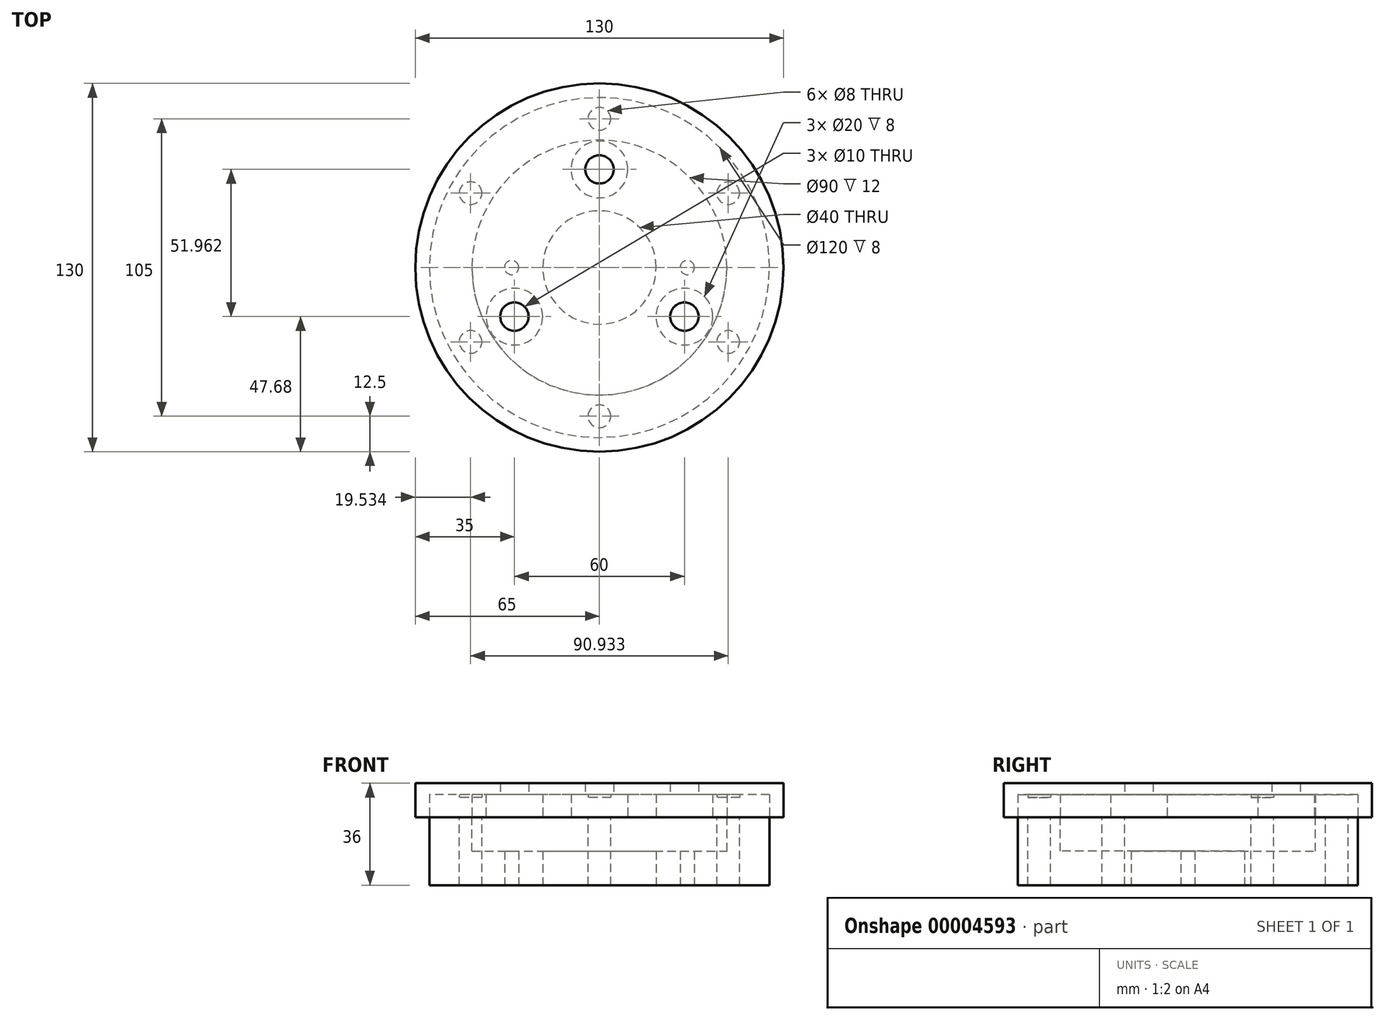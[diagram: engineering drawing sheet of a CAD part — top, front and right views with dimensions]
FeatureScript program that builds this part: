
annotation { "Feature Type Name" : "Feature", "Feature Type Description" : "" }
export const myFeature = defineFeature(function(context is Context, id is Id, definition is map)
    precondition{}
    {
        {
            var Q0;
            Q0=qCreatedBy(makeId("Top.planeOp"),FACE);
            var sketch = newSketch(context, id + "F0", { "sketchPlane" : qUnion([Q0])});
            skCircle(sketch, "E0", {"center": v(0, 0) * mm, "radius": 65 * mm});
            skLineSegment(sketch, "E1", {"start": v(0, 0) * mm, "end": v(0, 65) * mm, "construction": true});
            skLineSegment(sketch, "E2", {"start": v(0, 0) * mm, "end": v(56.3, -32.5) * mm, "construction": true});
            skLineSegment(sketch, "E3", {"start": v(0, 0) * mm, "end": v(-56.3, -32.5) * mm, "construction": true});
            skCircle(sketch, "E4", {"center": v(0, 0) * mm, "radius": 34.64 * mm, "construction": true});
            skCircle(sketch, "E5", {"center": v(0, 34.64) * mm, "radius": 5 * mm});
            skCircle(sketch, "E6", {"center": v(30, -17.32) * mm, "radius": 5 * mm});
            skCircle(sketch, "E7", {"center": v(-30, -17.32) * mm, "radius": 5 * mm});
            skCircle(sketch, "E8", {"center": v(0, 0) * mm, "radius": 60 * mm});
            skCircle(sketch, "E9", {"center": v(0, 0) * mm, "radius": 45 * mm});
            skCircle(sketch, "E10", {"center": v(-45.47, -26.25) * mm, "radius": 4 * mm});
            skCircle(sketch, "E11", {"center": v(0, 52.5) * mm, "radius": 4 * mm});
            skCircle(sketch, "E12", {"center": v(45.47, -26.25) * mm, "radius": 4 * mm});
            skCircle(sketch, "E13", {"center": v(0, 0) * mm, "radius": 52.5 * mm, "construction": true});
            skCircle(sketch, "E14", {"center": v(-52.5, 0) * mm, "radius": 7.5 * mm, "construction": true});
            skLineSegment(sketch, "E15", {"start": v(0, 0) * mm, "end": v(56.3, 32.5) * mm, "construction": true});
            skLineSegment(sketch, "E16", {"start": v(0, 0) * mm, "end": v(-56.3, 32.5) * mm, "construction": true});
            skLineSegment(sketch, "E17", {"start": v(0, 0) * mm, "end": v(0, -65) * mm, "construction": true});
            skCircle(sketch, "E18", {"center": v(45.47, 26.25) * mm, "radius": 4 * mm});
            skCircle(sketch, "E19", {"center": v(-45.47, 26.25) * mm, "radius": 4 * mm});
            skCircle(sketch, "E20", {"center": v(0, -52.5) * mm, "radius": 4 * mm});
            skCircle(sketch, "E21", {"center": v(30, -17.32) * mm, "radius": 10 * mm});
            skCircle(sketch, "E22", {"center": v(-30, -17.32) * mm, "radius": 10 * mm});
            skCircle(sketch, "E23", {"center": v(0, 34.64) * mm, "radius": 10 * mm});
            skSolve(sketch);
        }
        {
            var Q0;
            Q0=makeQuery(id+"F0.imprint","IMPRINT",FACE,{"disambiguationData":[TD([[makeQuery(id+"F0.imprint","IMPRINT",EDGE,{"derivedFrom":sQuery(id+"F0.wireOp",EDGE,"E0")}),1.0]])]});
            var Q1;
            Q1=makeQuery(id+"F0.imprint","IMPRINT",FACE,{"disambiguationData":[TD([[makeQuery(id+"F0.imprint","IMPRINT",EDGE,{"derivedFrom":sQuery(id+"F0.wireOp",EDGE,"E8")}),1.0]])]});
            var Q2;
            Q2=makeQuery(id+"F0.imprint","IMPRINT",FACE,{"disambiguationData":[TD([[makeQuery(id+"F0.imprint","IMPRINT",EDGE,{"derivedFrom":sQuery(id+"F0.wireOp",EDGE,"E5")}),-1.0]])]});
            var Q3;
            Q3=makeQuery(id+"F0.imprint","IMPRINT",FACE,{"disambiguationData":[TD([[makeQuery(id+"F0.imprint","IMPRINT",EDGE,{"derivedFrom":sQuery(id+"F0.wireOp",EDGE,"E10")}),1.0]])]});
            var Q4;
            Q4=makeQuery(id+"F0.imprint","IMPRINT",FACE,{"disambiguationData":[TD([[makeQuery(id+"F0.imprint","IMPRINT",EDGE,{"derivedFrom":sQuery(id+"F0.wireOp",EDGE,"E12")}),1.0]])]});
            var Q5;
            Q5=makeQuery(id+"F0.imprint","IMPRINT",FACE,{"disambiguationData":[TD([[makeQuery(id+"F0.imprint","IMPRINT",EDGE,{"derivedFrom":sQuery(id+"F0.wireOp",EDGE,"E11")}),1.0]])]});
            var Q6;
            Q6=makeQuery(id+"F0.imprint","IMPRINT",FACE,{"disambiguationData":[TD([[makeQuery(id+"F0.imprint","IMPRINT",EDGE,{"derivedFrom":sQuery(id+"F0.wireOp",EDGE,"E19")}),1.0]])]});
            var Q7;
            Q7=makeQuery(id+"F0.imprint","IMPRINT",FACE,{"disambiguationData":[TD([[makeQuery(id+"F0.imprint","IMPRINT",EDGE,{"derivedFrom":sQuery(id+"F0.wireOp",EDGE,"E18")}),1.0]])]});
            var Q8;
            Q8=makeQuery(id+"F0.imprint","IMPRINT",FACE,{"disambiguationData":[TD([[makeQuery(id+"F0.imprint","IMPRINT",EDGE,{"derivedFrom":sQuery(id+"F0.wireOp",EDGE,"E20")}),1.0]])]});
            var Q9;
            {var subQ0=sQuery(id+"F0.wireOp",EDGE,"E23");var subQ1=sQuery(id+"F0.wireOp",EDGE,"E9");var subQ3=makeQuery(id+"F0.imprint","INTERSECT",VERTEX,{"disambiguationData":[OD(0.0)],"derivedFrom":[subQ1,subQ0]});Q9=makeQuery(id+"F0.imprint","IMPRINT",FACE,{"disambiguationData":[TD([[makeQuery(id+"F0.imprint","IMPRINT",EDGE,{"disambiguationData":[TD([[subQ3,-1.0]])],"derivedFrom":subQ1}),1.0]])]});}
            var Q10;
            {var subQ0=sQuery(id+"F0.wireOp",EDGE,"E23");var subQ3=sQuery(id+"F0.wireOp",EDGE,"E9");var subQ4=makeQuery(id+"F0.imprint","INTERSECT",VERTEX,{"disambiguationData":[OD(0.0)],"derivedFrom":[subQ3,subQ0]});Q10=makeQuery(id+"F0.imprint","IMPRINT",FACE,{"disambiguationData":[TD([[makeQuery(id+"F0.imprint","IMPRINT",EDGE,{"disambiguationData":[TD([[subQ4,1.0]])],"derivedFrom":subQ3}),-1.0]])]});}
            var Q11;
            Q11=makeQuery(id+"F0.imprint","IMPRINT",FACE,{"disambiguationData":[TD([[makeQuery(id+"F0.imprint","IMPRINT",EDGE,{"derivedFrom":sQuery(id+"F0.wireOp",EDGE,"E7")}),-1.0]])]});
            var Q12;
            {var subQ0=sQuery(id+"F0.wireOp",EDGE,"E22");var subQ3=sQuery(id+"F0.wireOp",EDGE,"E9");var subQ6=makeQuery(id+"F0.imprint","INTERSECT",VERTEX,{"disambiguationData":[OD(0.0)],"derivedFrom":[subQ3,subQ0]});Q12=makeQuery(id+"F0.imprint","IMPRINT",FACE,{"disambiguationData":[TD([[makeQuery(id+"F0.imprint","IMPRINT",EDGE,{"disambiguationData":[TD([[subQ6,-1.0]])],"derivedFrom":subQ3}),-1.0]])]});}
            var Q13;
            Q13=makeQuery(id+"F0.imprint","IMPRINT",FACE,{"disambiguationData":[TD([[makeQuery(id+"F0.imprint","IMPRINT",EDGE,{"derivedFrom":sQuery(id+"F0.wireOp",EDGE,"E6")}),-1.0]])]});
            var Q14;
            {var subQ0=sQuery(id+"F0.wireOp",EDGE,"E21");var subQ3=sQuery(id+"F0.wireOp",EDGE,"E9");var subQ6=makeQuery(id+"F0.imprint","INTERSECT",VERTEX,{"disambiguationData":[OD(0.0)],"derivedFrom":[subQ3,subQ0]});Q14=makeQuery(id+"F0.imprint","IMPRINT",FACE,{"disambiguationData":[TD([[makeQuery(id+"F0.imprint","IMPRINT",EDGE,{"disambiguationData":[TD([[subQ6,-1.0]])],"derivedFrom":subQ3}),-1.0]])]});}
            var Q15;
            Q15=makeQuery(id+"F0.imprint","IMPRINT",FACE,{"disambiguationData":[TD([[makeQuery(id+"F0.imprint","IMPRINT",EDGE,{"derivedFrom":sQuery(id+"F0.wireOp",EDGE,"E9")}),1.0]])]});
            extrude(context, id + "F1", {"entities" : qUnion([Q0, Q1, Q2, Q3, Q4, Q5, Q6, Q7, Q8, Q9, Q10, Q11, Q12, Q13, Q14, Q15]), "depth" : 12 * mm});
        }
        {
            var Q0;
            Q0=makeQuery(id+"F0.imprint","IMPRINT",FACE,{"disambiguationData":[TD([[makeQuery(id+"F0.imprint","IMPRINT",EDGE,{"derivedFrom":sQuery(id+"F0.wireOp",EDGE,"E8")}),1.0]])]});
            extrude(context, id + "F2", {"entities" : qUnion([Q0]), "oppositeDirection" : true, "depth" : 24 * mm});
        }
        {
            var Q0;
            Q0=makeQuery(id+"F2.opExtrude","CAP_FACE",FACE,{"disambiguationData":[OSD([sQuery(id+"F0.wireOp",EDGE,"E8"),sQuery(id+"F0.wireOp",EDGE,"E9")])],"isStart":false});
            var sketch = newSketch(context, id + "F3", { "sketchPlane" : qUnion([Q0])});
            skCircle(sketch, "E24", {"center": v(-31, 0) * mm, "radius": 2.5 * mm});
            skCircle(sketch, "E25", {"center": v(31, 0) * mm, "radius": 2.5 * mm});
            skCircle(sketch, "E26", {"center": v(0, 0) * mm, "radius": 20 * mm});
            skCircle(sketch, "E27", {"center": v(0, 0) * mm, "radius": 45.5 * mm});
            skSolve(sketch);
        }
        {
            var Q0;
            Q0 = qSketchRegion(id + "F3", true);
            extrude(context, id + "F4", {"entities" : qUnion([Q0]), "operationType" : NewBodyOperationType.ADD, "oppositeDirection" : true, "depth" : 12 * mm});
        }
        {
            var Q0;
            Q0=makeQuery(id+"F0.imprint","IMPRINT",FACE,{"disambiguationData":[TD([[makeQuery(id+"F0.imprint","IMPRINT",EDGE,{"derivedFrom":sQuery(id+"F0.wireOp",EDGE,"E18")}),1.0]])]});
            var Q1;
            Q1=makeQuery(id+"F0.imprint","IMPRINT",FACE,{"disambiguationData":[TD([[makeQuery(id+"F0.imprint","IMPRINT",EDGE,{"derivedFrom":sQuery(id+"F0.wireOp",EDGE,"E11")}),1.0]])]});
            var Q2;
            Q2=makeQuery(id+"F0.imprint","IMPRINT",FACE,{"disambiguationData":[TD([[makeQuery(id+"F0.imprint","IMPRINT",EDGE,{"derivedFrom":sQuery(id+"F0.wireOp",EDGE,"E19")}),1.0]])]});
            var Q3;
            Q3=makeQuery(id+"F0.imprint","IMPRINT",FACE,{"disambiguationData":[TD([[makeQuery(id+"F0.imprint","IMPRINT",EDGE,{"derivedFrom":sQuery(id+"F0.wireOp",EDGE,"E10")}),1.0]])]});
            var Q4;
            Q4=makeQuery(id+"F0.imprint","IMPRINT",FACE,{"disambiguationData":[TD([[makeQuery(id+"F0.imprint","IMPRINT",EDGE,{"derivedFrom":sQuery(id+"F0.wireOp",EDGE,"E20")}),1.0]])]});
            var Q5;
            Q5=makeQuery(id+"F0.imprint","IMPRINT",FACE,{"disambiguationData":[TD([[makeQuery(id+"F0.imprint","IMPRINT",EDGE,{"derivedFrom":sQuery(id+"F0.wireOp",EDGE,"E12")}),1.0]])]});
            var Q6;
            Q6=sQuery(id+"F0.wireOp",EDGE,"E10");
            extrude(context, id + "F5", {"entities" : qUnion([Q0, Q1, Q2, Q3, Q4, Q5]), "operationType" : NewBodyOperationType.REMOVE, "surfaceEntities" : qUnion([Q6]), "depth" : (12 - 5) * mm});
        }
        {
            var Q0;
            Q0=makeQuery(id+"F0.imprint","IMPRINT",FACE,{"disambiguationData":[TD([[makeQuery(id+"F0.imprint","IMPRINT",EDGE,{"derivedFrom":sQuery(id+"F0.wireOp",EDGE,"E5")}),-1.0]])]});
            var Q1;
            {var subQ0=sQuery(id+"F0.wireOp",EDGE,"E23");var subQ3=sQuery(id+"F0.wireOp",EDGE,"E9");var subQ4=makeQuery(id+"F0.imprint","INTERSECT",VERTEX,{"disambiguationData":[OD(0.0)],"derivedFrom":[subQ3,subQ0]});Q1=makeQuery(id+"F0.imprint","IMPRINT",FACE,{"disambiguationData":[TD([[makeQuery(id+"F0.imprint","IMPRINT",EDGE,{"disambiguationData":[TD([[subQ4,1.0]])],"derivedFrom":subQ3}),-1.0]])]});}
            var Q2;
            Q2=makeQuery(id+"F0.imprint","IMPRINT",FACE,{"disambiguationData":[TD([[makeQuery(id+"F0.imprint","IMPRINT",EDGE,{"derivedFrom":sQuery(id+"F0.wireOp",EDGE,"E6")}),-1.0]])]});
            var Q3;
            {var subQ0=sQuery(id+"F0.wireOp",EDGE,"E21");var subQ3=sQuery(id+"F0.wireOp",EDGE,"E9");var subQ6=makeQuery(id+"F0.imprint","INTERSECT",VERTEX,{"disambiguationData":[OD(0.0)],"derivedFrom":[subQ3,subQ0]});Q3=makeQuery(id+"F0.imprint","IMPRINT",FACE,{"disambiguationData":[TD([[makeQuery(id+"F0.imprint","IMPRINT",EDGE,{"disambiguationData":[TD([[subQ6,-1.0]])],"derivedFrom":subQ3}),-1.0]])]});}
            var Q4;
            Q4=makeQuery(id+"F0.imprint","IMPRINT",FACE,{"disambiguationData":[TD([[makeQuery(id+"F0.imprint","IMPRINT",EDGE,{"derivedFrom":sQuery(id+"F0.wireOp",EDGE,"E7")}),-1.0]])]});
            var Q5;
            {var subQ0=sQuery(id+"F0.wireOp",EDGE,"E22");var subQ3=sQuery(id+"F0.wireOp",EDGE,"E9");var subQ6=makeQuery(id+"F0.imprint","INTERSECT",VERTEX,{"disambiguationData":[OD(0.0)],"derivedFrom":[subQ3,subQ0]});Q5=makeQuery(id+"F0.imprint","IMPRINT",FACE,{"disambiguationData":[TD([[makeQuery(id+"F0.imprint","IMPRINT",EDGE,{"disambiguationData":[TD([[subQ6,-1.0]])],"derivedFrom":subQ3}),-1.0]])]});}
            var Q6;
            {var subQ0=sQuery(id+"F0.wireOp",EDGE,"E22");var subQ1=sQuery(id+"F0.wireOp",EDGE,"E10");var subQ3=makeQuery(id+"F0.imprint","INTERSECT",VERTEX,{"disambiguationData":[OD(0.0)],"derivedFrom":[subQ1,subQ0]});Q6=makeQuery(id+"F0.imprint","IMPRINT",FACE,{"disambiguationData":[TD([[makeQuery(id+"F0.imprint","IMPRINT",EDGE,{"disambiguationData":[TD([[subQ3,1.0]])],"derivedFrom":subQ1}),1.0]])]});}
            var Q7;
            {var subQ0=sQuery(id+"F0.wireOp",EDGE,"E23");var subQ1=sQuery(id+"F0.wireOp",EDGE,"E11");var subQ3=makeQuery(id+"F0.imprint","INTERSECT",VERTEX,{"disambiguationData":[OD(0.0)],"derivedFrom":[subQ1,subQ0]});Q7=makeQuery(id+"F0.imprint","IMPRINT",FACE,{"disambiguationData":[TD([[makeQuery(id+"F0.imprint","IMPRINT",EDGE,{"disambiguationData":[TD([[subQ3,1.0]])],"derivedFrom":subQ1}),1.0]])]});}
            var Q8;
            {var subQ0=sQuery(id+"F0.wireOp",EDGE,"E21");var subQ1=sQuery(id+"F0.wireOp",EDGE,"E12");var subQ3=makeQuery(id+"F0.imprint","INTERSECT",VERTEX,{"disambiguationData":[OD(0.0)],"derivedFrom":[subQ1,subQ0]});Q8=makeQuery(id+"F0.imprint","IMPRINT",FACE,{"disambiguationData":[TD([[makeQuery(id+"F0.imprint","IMPRINT",EDGE,{"disambiguationData":[TD([[subQ3,1.0]])],"derivedFrom":subQ1}),1.0]])]});}
            var Q9;
            Q9=sQuery(id+"F0.wireOp",EDGE,"E23");
            extrude(context, id + "F6", {"entities" : qUnion([Q0, Q1, Q2, Q3, Q4, Q5, Q6, Q7, Q8]), "operationType" : NewBodyOperationType.REMOVE, "surfaceEntities" : qUnion([Q9]), "depth" : (12 - 4) * mm});
        }
    });
